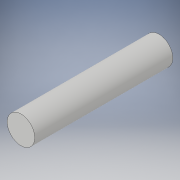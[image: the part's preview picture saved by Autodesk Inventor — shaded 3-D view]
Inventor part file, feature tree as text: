
AUTODESK INVENTOR PART (.ipt)
format: ipt  version: 2019 (Build 230136000, 136)  size: 90,112 bytes
history: native  units: mm
features: extrude x1, sketch x1
ambient origin geometry x8: Origin, YZ Plane, XZ Plane, XY Plane, X Axis, Y Axis, Z Axis, Center Point
bodies: Solid1 (feature_tree)
feature tree (2):
  extrude  "Extrusion1"  Depth=15.0mm TaperAngle=0.0deg
  sketch  "Sketch1"  dims[d0=3.0mm d1=15.0mm d2=0.0mm]
